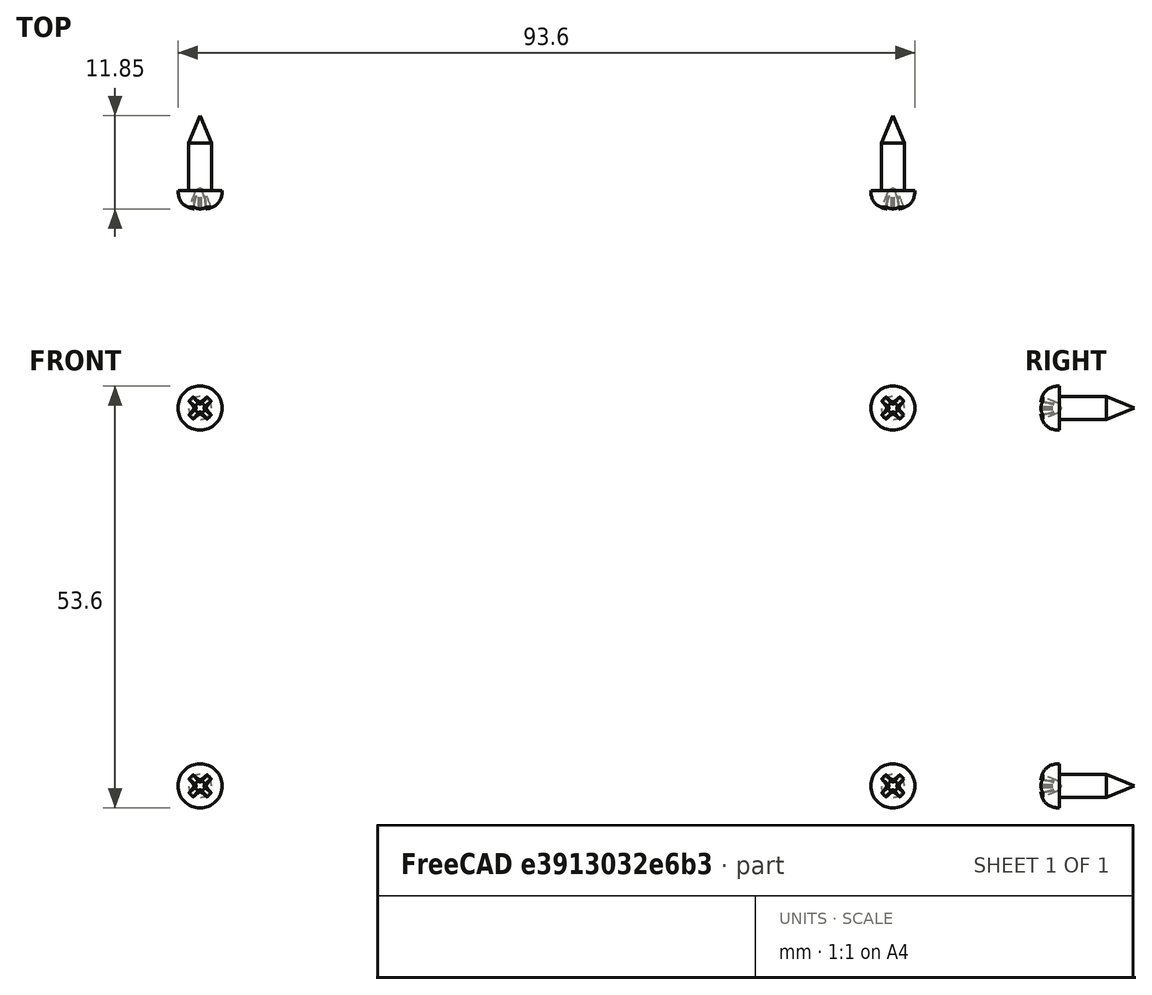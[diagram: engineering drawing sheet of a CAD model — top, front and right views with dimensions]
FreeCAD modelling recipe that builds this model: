
FCSTD DOCUMENT  (FreeCAD 1.0R39319 (Git))
Label: Assy_V3Connector_Board
License: All rights reserved
LicenseURL: https://en.wikipedia.org/wiki/All_rights_reserved
objects: TechDraw::DrawViewBalloon×6, Part::FeaturePython×4, TechDraw::DrawProjGroupItem×4, App::DocumentObjectGroup×3, TechDraw::DrawViewDimension×3, App::Link×2, TechDraw::DrawSVGTemplate×2, TechDraw::DrawPage×2, PartDesign::CoordinateSystem×1, App::FeaturePython×1, App::Part×1, Spreadsheet::Sheet×1, TechDraw::DrawViewSpreadsheet×1, TechDraw::DrawProjGroup×1
note: 11 computed .brp shape members not serialized (recipe doc carries the construction recipe); baked Part::Feature solids carry a one-line shape summary decoded from their .brp
EXTERNAL_REF file=../../Part/Print/ConnectorBoardv3_Carrier.FCStd obj=LCS_1
EXTERNAL_REF file=../../Part/Print/ConnectorBoardv3_Carrier.FCStd obj=Part
EXTERNAL_REF file=../../Part/Print/ConnectorBoardv3_Carrier.FCStd obj=LCS_2
EXTERNAL_REF file=../../Part/Purchase/V3_Connector_board.FCStd obj=LCS_1
EXTERNAL_REF file=../../Part/Purchase/V3_Connector_board.FCStd obj=V3_Connector_Only_1

FEATURE [App::DocumentObjectGroup] Parts
FEATURE [PartDesign::CoordinateSystem] LCS_Origin
  AttacherType = Attacher::AttachEngine3D
  AttachmentSupport = -> [X_Axis]
  MapMode = 2
FEATURE [App::DocumentObjectGroup] Constraints
FEATURE [App::FeaturePython] Variables  # WARN: FeaturePython — macro-defined, semantics opaque (R4)
  Type = App::PropertyContainer
FEATURE [App::DocumentObjectGroup] Configurations
FEATURE [App::Link] ConnectorBoardv3_Carrier
  AttachedBy = #LCS_1
  AttachedTo = Parent Assembly#LCS_Origin
  LinkedObject = -> <external ../../Part/Print/ConnectorBoardv3_Carrier.FCStd>#Part
  SolverId = Asm4EE
  expr: Placement = LCS_Origin.Placement * AttachmentOffset * ConnectorBoardv3_Carrier#LCS_1.Placement ^ -1
FEATURE [App::Link] V3_Connector_Only_1  label="V3 Connector Only 1"
  AttachedBy = #LCS_1
  AttachedTo = ConnectorBoardv3_Carrier#LCS_2
  AttachmentOffset = pos=(0,0,0) rot=(0.707107,-0.707107,0;3.14159rad)
  LinkPlacement = pos=(-50.0123,-11.5506,-30.0106) rot=(-0.57735,0.57735,-0.57735;4.18879rad)
  LinkedObject = -> <external ../../Part/Purchase/V3_Connector_board.FCStd>#V3_Connector_Only_1
  Placement = pos=(-50.0123,-11.5506,-30.0106) rot=(-0.57735,0.57735,-0.57735;4.18879rad)
  SolverId = Asm4EE
  expr: Placement = ConnectorBoardv3_Carrier.Placement * ConnectorBoardv3_Carrier#LCS_2.Placement * AttachmentOffset * V3_Connector_board#LCS_1.Placement ^ -1
FEATURE [Part::FeaturePython] Screw  label="ST2.9x9.5-Screw"  # WARN: FeaturePython — macro-defined, semantics opaque (R4)
  BaseObject = -> V3_Connector_Only_1 [Part__Feature388.Edge261]
  Diameter = 2
  Invert = false
  LeftHanded = false
  Length = 1
  LengthCustom = 9.5
  MatchOuter = false
  OffsetAngle = 0
  Placement = pos=(-44,-12.3124,-24) rot=(1,0,0;1.5708rad)
  Thread = false
  Type = 81
FEATURE [Part::FeaturePython] Screw001  label="ST2.9x9.5-Screw004"  # WARN: FeaturePython — macro-defined, semantics opaque (R4)
  BaseObject = -> V3_Connector_Only_1 [Part__Feature388.Edge17]
  Diameter = 2
  Invert = false
  LeftHanded = false
  Length = 1
  LengthCustom = 9.5
  MatchOuter = false
  OffsetAngle = 0
  Placement = pos=(44,-12.3124,-24) rot=(1,0,0;1.5708rad)
  Thread = false
  Type = 81
FEATURE [Part::FeaturePython] Screw002  label="ST2.9x9.5-Screw005"  # WARN: FeaturePython — macro-defined, semantics opaque (R4)
  BaseObject = -> V3_Connector_Only_1 [Part__Feature388.Edge18]
  Diameter = 2
  Invert = false
  LeftHanded = false
  Length = 1
  LengthCustom = 9.5
  MatchOuter = false
  OffsetAngle = 0
  Placement = pos=(44,-12.3124,24) rot=(1,0,0;1.5708rad)
  Thread = false
  Type = 81
FEATURE [Part::FeaturePython] Screw003  label="ST2.9x9.5-Screw006"  # WARN: FeaturePython — macro-defined, semantics opaque (R4)
  BaseObject = -> V3_Connector_Only_1 [Part__Feature388.Edge262]
  Diameter = 2
  Invert = false
  LeftHanded = false
  Length = 1
  LengthCustom = 9.5
  MatchOuter = false
  OffsetAngle = 0
  Placement = pos=(-44,-12.3124,24) rot=(1,0,0;1.5708rad)
  Thread = false
  Type = 81
FEATURE [App::Part] Assembly  label="Assy_V3Connector_Board"
  AssemblyType = Part::Link
  Group = -> [LCS_Origin,Constraints,Variables,Configurations,ConnectorBoardv3_Carrier,V3_Connector_Only_1,Screw,Screw001,Screw002,Screw003]
  Origin = -> Origin
  Type = Assembly
FEATURE [Spreadsheet::Sheet] Spreadsheet  label="BOM"
  cells = A1=3; B1=4; C1='M3x10 mm self-tapping screw; D1='5-10 mm; A2=2; B2=1; C2='ConnectorBoardv3; D2='-; A3=1; B3=1; C3='ConnectorBoardv3_Carrier; D3='-; E3='PETG or PLA; A4='Position; B4='Quantity; C4='Part; D4='Dimensions; E4='Material
FEATURE [TechDraw::DrawSVGTemplate] Template
  EditableTexts = approval_person=GitHub PR; creator=Stefan; date_of_issue=20.03.2026; document_type=Assembly Drawing; general_tolerances=na; identification_number=na; language_code=EN; part_material=na; revision_index=AAA; scale=1 : 1; sheet_number=1 / 1; title=Assy_V3Connector_Board
  Height = 297
  Orientation = 0
  Template = <userpath>/Documents/PiTrac/3D Printed Parts/Enclosure Version 3/Assets/PiTrac_A4_Portrait_ISO5457_minimal.svg
  Width = 210
FEATURE [TechDraw::DrawViewSpreadsheet] Sheet
  CellEnd = E4
  CellStart = A1
  Font = osifont
  LineWidth = 0.35
  LockPosition = false
  Rotation = 0
  ScaleType = 2
  Source = -> Spreadsheet
  Symbol = <blob: 4591 chars omitted>
  TextSize = 12
  X = 115.863
  Y = 88.338
FEATURE [TechDraw::DrawProjGroupItem] View  label="Front"
  CoarseView = false
  Direction = (0,-1,0)
  Focus = 100
  HardHidden = false
  IsoCount = 0
  IsoHidden = false
  IsoVisible = false
  LockPosition = true
  Perspective = false
  Rotation = 0
  RotationVector = (1,0,0)
  ScaleType = 2
  ScrubCount = 1
  SeamHidden = false
  SeamVisible = false
  SmoothHidden = false
  SmoothVisible = true
  Source = -> [Assembly]
  Type = 0
  X = 0
  XDirection = (1,0,0)
  Y = 0
FEATURE [TechDraw::DrawProjGroupItem] View001
  CoarseView = false
  Direction = (0.57735,-0.57735,-0.57735)
  Focus = 100
  HardHidden = false
  IsoCount = 0
  IsoHidden = false
  IsoVisible = false
  LockPosition = false
  Perspective = false
  Rotation = 0
  RotationVector = (1,0,0)
  Scale = 0.5
  ScaleType = 2
  ScrubCount = 1
  SeamHidden = false
  SeamVisible = false
  SmoothHidden = false
  SmoothVisible = true
  Source = -> [Assembly]
  Type = 0
  X = 158.895
  XDirection = (0.707107,0,0.707107)
  Y = 134.295
FEATURE [TechDraw::DrawViewBalloon] Balloon
  BubbleShape = 0
  EndType = 0
  EndTypeScale = 1
  KinkLength = 5
  LockPosition = false
  OriginX = -52.3797
  OriginY = -28.3457
  Rotation = 0
  ScaleType = 0
  ShapeScale = 1
  SourceView = -> View
  Text = 1
  TextWrapLen = -1
  X = -42.9122
  Y = -45
FEATURE [TechDraw::DrawViewBalloon] Balloon001
  BubbleShape = 0
  EndType = 0
  EndTypeScale = 1
  KinkLength = 5
  LockPosition = false
  OriginX = 21.9174
  OriginY = -1.30268
  Rotation = 0
  ScaleType = 0
  ShapeScale = 1
  SourceView = -> View
  Text = 2
  TextWrapLen = -1
  X = 31.9542
  Y = -45
FEATURE [TechDraw::DrawViewBalloon] Balloon002
  BubbleShape = 0
  EndType = 0
  EndTypeScale = 1
  KinkLength = 5
  LockPosition = false
  OriginX = -43.5551
  OriginY = 18.9084
  Rotation = 0
  ScaleType = 0
  ShapeScale = 1
  SourceView = -> View
  Text = 3
  TextWrapLen = -1
  X = -23.5551
  Y = 45
FEATURE [TechDraw::DrawViewBalloon] Balloon003
  BubbleShape = 0
  EndType = 0
  EndTypeScale = 1
  KinkLength = 5
  LockPosition = false
  OriginX = 44.2277
  OriginY = 19.5981
  Rotation = 0
  ScaleType = 0
  ShapeScale = 1
  SourceView = -> View
  Text = 3
  TextWrapLen = -1
  X = 64.2277
  Y = 45
FEATURE [TechDraw::DrawViewBalloon] Balloon005
  BubbleShape = 0
  EndType = 0
  EndTypeScale = 1
  KinkLength = 5
  LockPosition = false
  OriginX = -43.4289
  OriginY = -28.7897
  Rotation = 0
  ScaleType = 0
  ShapeScale = 1
  SourceView = -> View
  Text = 3
  TextWrapLen = -1
  X = -15.4584
  Y = -45
FEATURE [TechDraw::DrawViewBalloon] Balloon006
  BubbleShape = 0
  EndType = 0
  EndTypeScale = 1
  KinkLength = 5
  LockPosition = false
  OriginX = 44.6905
  OriginY = -29.4843
  Rotation = 0
  ScaleType = 0
  ShapeScale = 1
  SourceView = -> View
  Text = 3
  TextWrapLen = -1
  X = 64.6905
  Y = -9.48434
FEATURE [TechDraw::DrawProjGroupItem] ProjItem  label="Left"
  CoarseView = false
  Direction = (-1,-1e-16,0)
  Focus = 100
  HardHidden = false
  IsoCount = 0
  IsoHidden = false
  IsoVisible = false
  LockPosition = false
  Perspective = false
  Rotation = 0
  RotationVector = (1,0,0)
  ScaleType = 0
  ScrubCount = 1
  SeamHidden = false
  SeamVisible = false
  SmoothHidden = false
  SmoothVisible = true
  Source = -> [Assembly]
  Type = 1
  X = 26.9737
  XDirection = (1e-16,-1,0)
  Y = 0
FEATURE [TechDraw::DrawProjGroup] ProjGroup
  Anchor = -> View
  AutoDistribute = true
  LockPosition = false
  ProjectionType = 0
  Rotation = 0
  ScaleType = 0
  Source = -> [Assembly]
  Views = -> [View,ProjItem]
  X = 83.6926
  Y = 220.778
  spacingX = 15
  spacingY = 15
FEATURE [TechDraw::DrawViewDimension] Dimension
  AngleOverride = false
  Arbitrary = false
  ArbitraryTolerances = false
  BoxCorners = (2) [(-55,-35.0053,-1e-07),(55,35.0053,1e-07)]
  EqualTolerance = true
  ExtensionAngle = 0
  FormatSpec = %.2w
  FormatSpecOverTolerance = %+.2w
  FormatSpecUnderTolerance = %+.2w
  Inverted = false
  LineAngle = 0
  LockPosition = false
  MeasureType = 1
  OverTolerance = 0
  References2D = -> [View]
  Rotation = 0
  ScaleType = 0
  TheoreticalExact = false
  Type = 0
  UnderTolerance = 0
  X = 0
  Y = -54.1451
FEATURE [TechDraw::DrawViewDimension] Dimension001
  AngleOverride = false
  Arbitrary = false
  ArbitraryTolerances = false
  BoxCorners = (2) [(-11.9737,-35.0053,-1e-07),(11.9737,35.0053,1e-07)]
  EqualTolerance = true
  ExtensionAngle = 0
  FormatSpec = %.2w
  FormatSpecOverTolerance = %+.2w
  FormatSpecUnderTolerance = %+.2w
  Inverted = false
  LineAngle = 0
  LockPosition = false
  MeasureType = 1
  OverTolerance = 0
  References2D = -> [ProjItem]
  Rotation = 0
  ScaleType = 0
  TheoreticalExact = false
  Type = 0
  UnderTolerance = 0
  X = 18.3809
  Y = 0.005286
FEATURE [TechDraw::DrawViewDimension] Dimension002
  AngleOverride = false
  Arbitrary = false
  ArbitraryTolerances = false
  BoxCorners = (2) [(-11.9737,-35.0053,-1e-07),(11.9737,35.0053,1e-07)]
  EqualTolerance = true
  ExtensionAngle = 0
  FormatSpec = %.2w
  FormatSpecOverTolerance = %+.2w
  FormatSpecUnderTolerance = %+.2w
  Inverted = false
  LineAngle = 0
  LockPosition = false
  MeasureType = 1
  OverTolerance = 0
  References2D = -> [ProjItem]
  Rotation = 0
  ScaleType = 0
  TheoreticalExact = false
  Type = 0
  UnderTolerance = 0
  X = -0.8
  Y = 50.6191
FEATURE [TechDraw::DrawPage] Page
  KeepUpdated = true
  NextBalloonIndex = 8
  ProjectionType = 0
  Template = -> Template
  Views = -> [Sheet,View001,Balloon,Balloon001,Balloon002,Balloon003,Balloon005,Balloon006,ProjGroup,Dimension,Dimension001,Dimension002]
FEATURE [TechDraw::DrawSVGTemplate] Template001
  Height = 210
  Orientation = 1
  Template = C:/Program Files/FreeCAD 1.0/data/Mod/TechDraw/Templates/Default_Template_A4_Landscape.svg
  Width = 297
FEATURE [TechDraw::DrawProjGroupItem] View002
  CoarseView = false
  Direction = (0.57735,-0.57735,-0.57735)
  Focus = 100
  HardHidden = false
  IsoCount = 0
  IsoHidden = false
  IsoVisible = false
  LockPosition = false
  Perspective = false
  Rotation = 0
  RotationVector = (1,0,0)
  Scale = 2
  ScaleType = 2
  ScrubCount = 1
  SeamHidden = false
  SeamVisible = false
  SmoothHidden = false
  SmoothVisible = true
  Source = -> [Assembly]
  Type = 0
  X = 148.5
  XDirection = (0.707107,0,0.707107)
  Y = 105
FEATURE [TechDraw::DrawPage] Page001
  KeepUpdated = true
  NextBalloonIndex = 1
  ProjectionType = 0
  Template = -> Template001
  Views = -> [View002]

RESOLVED EXTERNAL PARTS (link-assembly join: the EXTERNAL_REF files above that resolve inside this repo's crawl, each included once):
---- part ../../Part/Print/ConnectorBoardv3_Carrier.FCStd = doc fcstd_a96b8e3c4932 ----
FCSTD DOCUMENT  (FreeCAD 1.0R39319 (Git))
Label: ConnectorBoardv3_Carrier
License: All rights reserved
LicenseURL: https://en.wikipedia.org/wiki/All_rights_reserved
objects: Sketcher::SketchObject×8, PartDesign::Pocket×4, PartDesign::Pad×3, PartDesign::Fillet×3, PartDesign::Mirrored×2, PartDesign::LinearPattern×2, PartDesign::CoordinateSystem×2, PartDesign::Hole×1, PartDesign::Body×1, App::Part×1
note: 60 computed .brp shape members not serialized (recipe doc carries the construction recipe); baked Part::Feature solids carry a one-line shape summary decoded from their .brp

FEATURE [Sketcher::SketchObject] Sketch
  ArcFitTolerance = 1e-06
  AttachmentSupport = -> [XZ_Plane001]
  FullyConstrained = true
  MakeInternals = false
  MapMode = 5
  Placement = pos=(0,0,0) rot=(1,0,0;1.5708rad)
  sketch-geometry (4):
    g0: LineSegment StartX=0 StartY=30 StartZ=0 EndX=0 EndY=0 EndZ=0
    g1: LineSegment StartX=0 StartY=0 StartZ=0 EndX=55 EndY=0 EndZ=0
    g2: LineSegment StartX=55 StartY=0 StartZ=0 EndX=55 EndY=30 EndZ=0
    g3: LineSegment StartX=55 StartY=30 StartZ=0 EndX=0 EndY=30 EndZ=0
  constraints (12):
    c: Coincident(g0,g1)
    c: Coincident(g1,g2)
    c: Coincident(g2,g3)
    c: Coincident(g3,g0)
    c: Vertical(g0)
    c: Vertical(g2)
    c: Distance(g-1,g2) = 55
    c: Distance(g0,g1) = 30
    c: Horizontal(g1)
    c: Horizontal(g3)
    c: DistanceX(g-1,g0) = 0
    c: DistanceY(g-1,g0) = 0
FEATURE [PartDesign::Pad] Pad
  Direction = (0,-1,2e-16)
  Length = 2.5
  Length2 = 10
  Placement = pos=(0,0,0) rot=(1,0,0;1.5708rad)
  Profile = -> Sketch
  ReferenceAxis = -> Sketch [N_Axis]
  Refine = true
  Suppressed = false
  Type = 0
FEATURE [Sketcher::SketchObject] Sketch001
  ArcFitTolerance = 1e-06
  AttachmentSupport = -> [XZ_Plane001]
  FullyConstrained = true
  MakeInternals = false
  MapMode = 5
  Placement = pos=(0,0,0) rot=(1,0,0;1.5708rad)
  sketch-geometry (1):
    g0: Circle CenterX=44 CenterY=24 CenterZ=0 NormalX=0 NormalY=0 NormalZ=1 AngleXU=0 Radius=3.75
  constraints (3):
    c: Diameter(g0) = 7.5
    c: DistanceX(g-1,g0) = 44
    c: Distance(g0,g-1) = 24
FEATURE [PartDesign::Pad] Pad001
  BaseFeature = -> Pad
  Direction = (0,-1,2e-16)
  Length = 11.5
  Length2 = 10
  Placement = pos=(0,0,0) rot=(1,0,0;1.5708rad)
  Profile = -> Sketch001
  ReferenceAxis = -> Sketch001 [N_Axis]
  Refine = true
  Suppressed = false
  Type = 0
FEATURE [PartDesign::Hole] Hole
  BaseFeature = -> Pad001
  CustomThreadClearance = 0
  Depth = 128.667
  DepthType = 1
  Diameter = 2.3
  DrillForDepth = false
  DrillPoint = 1
  DrillPointAngle = 118
  HoleCutCountersinkAngle = 90
  HoleCutCustomValues = false
  HoleCutDepth = 0
  HoleCutDiameter = 6.1
  HoleCutType = 0
  ModelThread = false
  Placement = pos=(0,0,0) rot=(1,0,0;1.5708rad)
  Profile = -> Pad001 [Face7]
  Refine = true
  Suppressed = false
  Tapered = false
  TaperedAngle = 90
  ThreadClass = 0
  ThreadDepth = 128.667
  ThreadDepthType = 0
  ThreadDirection = 0
  ThreadFit = 0
  ThreadSize = 0
  ThreadType = 0
  Threaded = false
  UseCustomThreadClearance = false
FEATURE [PartDesign::Fillet] Fillet
  Base = -> Hole [Edge5]
  BaseFeature = -> Hole
  Placement = pos=(0,0,0) rot=(1,0,0;1.5708rad)
  Radius = 3.5
  Refine = true
  SupportTransform = false
  Suppressed = false
  UseAllEdges = false
FEATURE [Sketcher::SketchObject] Sketch002
  ArcFitTolerance = 1e-06
  AttachmentSupport = -> [XZ_Plane001]
  FullyConstrained = true
  MakeInternals = false
  MapMode = 5
  Placement = pos=(0,0,0) rot=(1,0,0;1.5708rad)
  sketch-geometry (4):
    g0: ArcOfCircle CenterX=0 CenterY=0 CenterZ=0 NormalX=0 NormalY=0 NormalZ=1 AngleXU=0 Radius=4 StartAngle=1.5708 EndAngle=4.71239
    g1: ArcOfCircle CenterX=46 CenterY=-2e-16 CenterZ=0 NormalX=0 NormalY=0 NormalZ=1 AngleXU=0 Radius=4 StartAngle=4.71239 EndAngle=7.85398
    g2: LineSegment StartX=-6e-16 StartY=4 StartZ=0 EndX=46 EndY=4 EndZ=0
    g3: LineSegment StartX=-7e-16 StartY=-4 StartZ=0 EndX=46 EndY=-4 EndZ=0
  constraints (9):
    c: Tangent(g0,g2) = 1.5708
    c: Tangent(g0,g3) = -1.5708
    c: Tangent(g1,g2) = 1.5708
    c: Tangent(g1,g3) = -1.5708
    c: Equal(g0,g1)
    c: Horizontal(g3)
    c: Coincident(g0,g-1)
    c: DistanceY(g0,g0) = 4
    c: DistanceX(g3,g3) = 46
FEATURE [PartDesign::Pocket] Pocket
  BaseFeature = -> Fillet
  Direction = (0,1,-2e-16)
  Length = 5
  Length2 = 5
  Placement = pos=(0,0,0) rot=(1,0,0;1.5708rad)
  Profile = -> Sketch002
  ReferenceAxis = -> Sketch002 [N_Axis]
  Refine = true
  Reversed = true
  Suppressed = false
  Type = 1
FEATURE [PartDesign::Mirrored] Mirrored
  BaseFeature = -> Pocket
  MirrorPlane = -> XY_Plane001
  Placement = pos=(0,0,0) rot=(1,0,0;1.5708rad)
  Refine = true
  Suppressed = false
  TransformMode = 1
FEATURE [PartDesign::LinearPattern] LinearPattern
  BaseFeature = -> Mirrored
  Direction = -> Z_Axis001
  Length = 16
  Mode = 0
  Occurrences = 2
  Offset = 16
  Originals = -> [Pocket]
  Placement = pos=(0,0,0) rot=(1,0,0;1.5708rad)
  Refine = true
  Suppressed = false
  TransformMode = 0
FEATURE [PartDesign::LinearPattern] LinearPattern001
  BaseFeature = -> LinearPattern
  Direction = -> Z_Axis001
  Length = 16
  Mode = 0
  Occurrences = 2
  Offset = 16
  Originals = -> [Pocket]
  Placement = pos=(0,0,0) rot=(1,0,0;1.5708rad)
  Refine = true
  Reversed = true
  Suppressed = false
  TransformMode = 0
FEATURE [PartDesign::Mirrored] Mirrored001
  BaseFeature = -> LinearPattern001
  MirrorPlane = -> YZ_Plane001
  Placement = pos=(0,0,0) rot=(1,0,0;1.5708rad)
  Refine = true
  Suppressed = false
  TransformMode = 1
FEATURE [Sketcher::SketchObject] Sketch003
  ArcFitTolerance = 1e-06
  AttachmentSupport = -> [Mirrored001]
  ExternalGeometry = -> [Mirrored001]
  FullyConstrained = true
  MakeInternals = false
  MapMode = 5
  Placement = pos=(0,-2.5,0) rot=(1,0,0;1.5708rad)
  sketch-geometry (8):
    g0: LineSegment StartX=-50 StartY=40 StartZ=0 EndX=-50 EndY=30 EndZ=0
    g1: LineSegment StartX=-50 StartY=30 StartZ=0 EndX=-30 EndY=30 EndZ=0
    g2: LineSegment StartX=-30 StartY=30 StartZ=0 EndX=-30 EndY=40 EndZ=0
    g3: LineSegment StartX=-30 StartY=40 StartZ=0 EndX=-50 EndY=40 EndZ=0
    g4: LineSegment StartX=30 StartY=40 StartZ=0 EndX=30 EndY=30 EndZ=0
    g5: LineSegment StartX=30 StartY=30 StartZ=0 EndX=50 EndY=30 EndZ=0
    g6: LineSegment StartX=50 StartY=30 StartZ=0 EndX=50 EndY=40 EndZ=0
    g7: LineSegment StartX=50 StartY=40 StartZ=0 EndX=30 EndY=40 EndZ=0
  constraints (23):
    c: Coincident(g0,g1)
    c: Coincident(g1,g2)
    c: Coincident(g2,g3)
    c: Coincident(g3,g0)
    c: Vertical(g0)
    c: Vertical(g2)
    c: Horizontal(g1)
    c: Horizontal(g3)
    c: Coincident(g4,g5)
    c: Coincident(g5,g6)
    c: Coincident(g6,g7)
    c: Coincident(g7,g4)
    c: Vertical(g4)
    c: Vertical(g6)
    c: Horizontal(g5)
    c: Horizontal(g7)
    c: Distance(g1,g3) = 10
    c: Distance(g5,g7) = 10
    c: Distance(g2,g0) = 20
    c: Distance(g6,g4) = 20
    c: PointOnObject(g1,g-3)
    c: DistanceX(g0,g6) = 100
    c: Symmetric(g2,g4,g-2)
FEATURE [PartDesign::Pad] Pad002
  BaseFeature = -> Mirrored001
  Direction = (0,-1,2e-16)
  Length = 10
  Length2 = 10
  Placement = pos=(0,0,0) rot=(1,0,0;1.5708rad)
  Profile = -> Sketch003
  ReferenceAxis = -> Sketch003 [N_Axis]
  Refine = true
  Suppressed = false
  Type = 3
  UpToFace = -> Mirrored001 [Face8]
FEATURE [Sketcher::SketchObject] Sketch004
  ArcFitTolerance = 1e-06
  AttachmentSupport = -> [Pad002]
  ExternalGeometry = -> [Pad002]
  FullyConstrained = true
  MakeInternals = false
  MapMode = 5
  Placement = pos=(0,-2.5,8e-16) rot=(1,0,0;1.5708rad)
  sketch-geometry (6):
    g0: Circle CenterX=-46.458 CenterY=36.5 CenterZ=0 NormalX=0 NormalY=0 NormalZ=1 AngleXU=0 Radius=1.5
    g1: Circle CenterX=-40.9807 CenterY=36 CenterZ=0 NormalX=0 NormalY=0 NormalZ=1 AngleXU=0 Radius=2
    g2: Circle CenterX=-34.5 CenterY=35.5 CenterZ=0 NormalX=0 NormalY=0 NormalZ=1 AngleXU=0 Radius=2.5
    g3: Circle CenterX=45.458 CenterY=35.5 CenterZ=0 NormalX=0 NormalY=0 NormalZ=1 AngleXU=0 Radius=2.5
    g4: Circle CenterX=38.9772 CenterY=36 CenterZ=0 NormalX=0 NormalY=0 NormalZ=1 AngleXU=0 Radius=2
    g5: Circle CenterX=33.5 CenterY=36.5 CenterZ=0 NormalX=0 NormalY=0 NormalZ=1 AngleXU=0 Radius=1.5
  constraints (18):
    c: Diameter(g2) = 5
    c: Diameter(g1) = 4
    c: Diameter(g0) = 3
    c: Distance(g2,g-5) = 2
    c: Distance(g1,g-5) = 2
    c: Distance(g0,g-5) = 2
    c: Distance(g2,g-3) = 2
    c: Distance(g1,g2) = 2
    c: Distance(g0,g1) = 2
    c: Diameter(g3) = 5
    c: Diameter(g4) = 4
    c: Diameter(g5) = 3
    c: Distance(g3,g-6) = 2
    c: Distance(g4,g-6) = 2
    c: Distance(g5,g-6) = 2
    c: Distance(g5,g-7) = 2
    c: Distance(g5,g4) = 2
    c: Distance(g4,g3) = 2
FEATURE [PartDesign::Pocket] Pocket001
  BaseFeature = -> Pad002
  Direction = (0,1,-2e-16)
  Length = 5
  Length2 = 5
  Placement = pos=(0,0,0) rot=(1,0,0;1.5708rad)
  Profile = -> Sketch004
  ReferenceAxis = -> Sketch004 [N_Axis]
  Refine = true
  Suppressed = false
  Type = 0
FEATURE [Sketcher::SketchObject] Sketch005
  ArcFitTolerance = 1e-06
  AttachmentSupport = -> [Pocket001]
  ExternalGeometry = -> [Pocket001]
  FullyConstrained = true
  MakeInternals = false
  MapMode = 5
  Placement = pos=(0,-2.5,8e-16) rot=(1,0,0;1.5708rad)
  sketch-geometry (24):
    g0: LineSegment StartX=-35.75 StartY=40 StartZ=0 EndX=-35.75 EndY=35.5 EndZ=0
    g1: LineSegment StartX=-35.75 StartY=35.5 StartZ=0 EndX=-33.25 EndY=35.5 EndZ=0
    g2: LineSegment StartX=-33.25 StartY=35.5 StartZ=0 EndX=-33.25 EndY=40 EndZ=0
    g3: LineSegment StartX=-33.25 StartY=40 StartZ=0 EndX=-35.75 EndY=40 EndZ=0
    g4: LineSegment StartX=-41.9807 StartY=40 StartZ=0 EndX=-41.9807 EndY=36 EndZ=0
    g5: LineSegment StartX=-41.9807 StartY=36 StartZ=0 EndX=-39.9807 EndY=36 EndZ=0
    g6: LineSegment StartX=-39.9807 StartY=36 StartZ=0 EndX=-39.9807 EndY=40 EndZ=0
    g7: LineSegment StartX=-39.9807 StartY=40 StartZ=0 EndX=-41.9807 EndY=40 EndZ=0
    g8: LineSegment StartX=-47.208 StartY=40 StartZ=0 EndX=-47.208 EndY=36.5 EndZ=0
    g9: LineSegment StartX=-47.208 StartY=36.5 StartZ=0 EndX=-45.708 EndY=36.5 EndZ=0
    g10: LineSegment StartX=-45.708 StartY=36.5 StartZ=0 EndX=-45.708 EndY=40 EndZ=0
    g11: LineSegment StartX=-45.708 StartY=40 StartZ=0 EndX=-47.208 EndY=40 EndZ=0
    g12: LineSegment StartX=32.75 StartY=40 StartZ=0 EndX=32.75 EndY=36.5 EndZ=0
    g13: LineSegment StartX=32.75 StartY=36.5 StartZ=0 EndX=34.25 EndY=36.5 EndZ=0
    g14: LineSegment StartX=34.25 StartY=36.5 StartZ=0 EndX=34.25 EndY=40 EndZ=0
    g15: LineSegment StartX=34.25 StartY=40 StartZ=0 EndX=32.75 EndY=40 EndZ=0
    g16: LineSegment StartX=37.9772 StartY=40 StartZ=0 EndX=37.9772 EndY=36 EndZ=0
    g17: LineSegment StartX=37.9772 StartY=36 StartZ=0 EndX=39.9772 EndY=36 EndZ=0
    g18: LineSegment StartX=39.9772 StartY=36 StartZ=0 EndX=39.9772 EndY=40 EndZ=0
    g19: LineSegment StartX=39.9772 StartY=40 StartZ=0 EndX=37.9772 EndY=40 EndZ=0
    g20: LineSegment StartX=44.208 StartY=40 StartZ=0 EndX=44.208 EndY=35.5 EndZ=0
    g21: LineSegment StartX=44.208 StartY=35.5 StartZ=0 EndX=46.708 EndY=35.5 EndZ=0
    g22: LineSegment StartX=46.708 StartY=35.5 StartZ=0 EndX=46.708 EndY=40 EndZ=0
    g23: LineSegment StartX=46.708 StartY=40 StartZ=0 EndX=44.208 EndY=40 EndZ=0
  constraints (66):
    c: Coincident(g0,g1)
    c: Coincident(g1,g2)
    c: Coincident(g2,g3)
    c: Coincident(g3,g0)
    c: Vertical(g0)
    c: Vertical(g2)
    c: Horizontal(g1)
    c: Horizontal(g3)
    c: Coincident(g4,g5)
    c: Coincident(g5,g6)
    c: Coincident(g6,g7)
    c: Coincident(g7,g4)
    c: Vertical(g4)
    c: Vertical(g6)
    c: Horizontal(g5)
    c: Horizontal(g7)
    c: Coincident(g8,g9)
    c: Coincident(g9,g10)
    c: Coincident(g10,g11)
    c: Coincident(g11,g8)
    c: Vertical(g8)
    c: Vertical(g10)
    c: Horizontal(g9)
    c: Horizontal(g11)
    c: PointOnObject(g2,g-3)
    c: PointOnObject(g6,g-3)
    c: PointOnObject(g10,g-3)
    c: Symmetric(g8,g9,g-6)
    c: Symmetric(g4,g5,g-5)
    c: Symmetric(g0,g1,g-4)
    c: Distance(g3,g3) = 2.5
    c: DistanceX(g7,g7) = 2
    c: DistanceX(g11,g11) = 1.5
    c: Coincident(g12,g13)
    c: Coincident(g13,g14)
    c: Coincident(g14,g15)
    c: Coincident(g15,g12)
    c: Vertical(g12)
    c: Vertical(g14)
    c: Horizontal(g13)
    c: Horizontal(g15)
    c: PointOnObject(g12,g-7)
    c: Coincident(g16,g17)
    c: Coincident(g17,g18)
    c: Coincident(g18,g19)
    c: Coincident(g19,g16)
    c: Vertical(g16)
    c: Vertical(g18)
    c: Horizontal(g17)
    c: Horizontal(g19)
    c: PointOnObject(g16,g-7)
    c: Coincident(g20,g21)
    c: Coincident(g21,g22)
    c: Coincident(g22,g23)
    c: Coincident(g23,g20)
    c: Vertical(g20)
    c: Vertical(g22)
    c: Horizontal(g21)
    c: Horizontal(g23)
    c: PointOnObject(g20,g-7)
    c: Symmetric(g12,g13,g-8)
    c: Symmetric(g16,g17,g-9)
    c: Symmetric(g20,g21,g-10)
    c: DistanceX(g23,g23) = 2.5
    c: Distance(g19,g19) = 2
    c: DistanceX(g15,g15) = 1.5
FEATURE [PartDesign::Pocket] Pocket002
  BaseFeature = -> Pocket001
  Direction = (0,1,-2e-16)
  Length = 5
  Length2 = 5
  Placement = pos=(0,0,0) rot=(1,0,0;1.5708rad)
  Profile = -> Sketch005
  ReferenceAxis = -> Sketch005 [N_Axis]
  Refine = true
  Suppressed = false
  Type = 0
FEATURE [PartDesign::Fillet] Fillet001
  Base = -> Pocket002 [Edge3,Edge1]
  BaseFeature = -> Pocket002
  Placement = pos=(0,0,0) rot=(1,0,0;1.5708rad)
  Radius = 3.5
  Refine = true
  SupportTransform = false
  Suppressed = false
  UseAllEdges = false
FEATURE [PartDesign::Fillet] Fillet002
  Base = -> Fillet001 [Edge141,Edge167,Edge158,Edge165,Edge157,Edge150,Edge149,Edge169,Edge137,Edge138,Edge143,Edge151,Edge153,Edge159,Edge161,Edge163]
  BaseFeature = -> Fillet001
  Placement = pos=(0,0,0) rot=(1,0,0;1.5708rad)
  Radius = 1
  Refine = true
  SupportTransform = false
  Suppressed = false
  UseAllEdges = false
FEATURE [Sketcher::SketchObject] Sketch006
  ArcFitTolerance = 1e-06
  AttachmentSupport = -> [Fillet002]
  FullyConstrained = true
  MakeInternals = false
  MapMode = 5
  Placement = pos=(0,-2.5,8e-16) rot=(1,0,0;1.5708rad)
FEATURE [Sketcher::SketchObject] Sketch007
  ArcFitTolerance = 1e-06
  AttachmentSupport = -> [Fillet002]
  ExternalGeometry = -> [Fillet002]
  FullyConstrained = true
  MakeInternals = false
  MapMode = 5
  Placement = pos=(0,-2.5,8e-16) rot=(1,0,0;1.5708rad)
  sketch-geometry (20):
    g0: LineSegment StartX=-43.4807 StartY=30.5 StartZ=0 EndX=-41.4807 EndY=30.5 EndZ=0
    g1: LineSegment StartX=-41.4807 StartY=30.5 StartZ=0 EndX=-41.4807 EndY=32.5 EndZ=0
    g2: LineSegment StartX=-41.4807 StartY=32.5 StartZ=0 EndX=-40.4807 EndY=32.5 EndZ=0
    g3: LineSegment StartX=-40.4807 StartY=32.5 StartZ=0 EndX=-40.4807 EndY=30.5 EndZ=0
    g4: LineSegment StartX=-40.4807 StartY=30.5 StartZ=0 EndX=-38.4807 EndY=30.5 EndZ=0
    g5: LineSegment StartX=-38.4807 StartY=30.5 StartZ=0 EndX=-38.4807 EndY=29.5 EndZ=0
    g6: LineSegment StartX=-38.4807 StartY=29.5 StartZ=0 EndX=-40.4807 EndY=29.5 EndZ=0
    g7: LineSegment StartX=-40.4807 StartY=29.5 StartZ=0 EndX=-40.4807 EndY=27.5 EndZ=0
    g8: LineSegment StartX=-40.4807 StartY=27.5 StartZ=0 EndX=-41.4807 EndY=27.5 EndZ=0
    g9: LineSegment StartX=-41.4807 StartY=27.5 StartZ=0 EndX=-41.4807 EndY=29.5 EndZ=0
    g10: LineSegment StartX=-41.4807 StartY=29.5 StartZ=0 EndX=-43.4807 EndY=29.5 EndZ=0
    g11: LineSegment StartX=-43.4807 StartY=29.5 StartZ=0 EndX=-43.4807 EndY=30.5 EndZ=0
    g12: LineSegment [constr] StartX=-43.4807 StartY=30 StartZ=0 EndX=-38.4807 EndY=30 EndZ=0
    g13: LineSegment [constr] StartX=-40.9807 StartY=32.5 StartZ=0 EndX=-40.9807 EndY=27.5 EndZ=0
    g14: LineSegment StartX=36.4772 StartY=30.5 StartZ=0 EndX=36.4772 EndY=29.5 EndZ=0
    g15: LineSegment StartX=36.4772 StartY=29.5 StartZ=0 EndX=41.4772 EndY=29.5 EndZ=0
    g16: LineSegment StartX=41.4772 StartY=29.5 StartZ=0 EndX=41.4772 EndY=30.5 EndZ=0
    g17: LineSegment StartX=41.4772 StartY=30.5 StartZ=0 EndX=36.4772 EndY=30.5 EndZ=0
    g18: LineSegment [constr] StartX=36.4772 StartY=30 StartZ=0 EndX=41.4772 EndY=30 EndZ=0
    g19: LineSegment [constr] StartX=38.9772 StartY=30.5 StartZ=0 EndX=38.9772 EndY=29.5 EndZ=0
  constraints (56):
    c: Horizontal(g0)
    c: Coincident(g0,g1)
    c: Vertical(g1)
    c: Coincident(g1,g2)
    c: Coincident(g2,g3)
    c: Vertical(g3)
    c: Coincident(g3,g4)
    c: Horizontal(g4)
    c: Coincident(g4,g5)
    c: Coincident(g5,g6)
    c: Horizontal(g6)
    c: Coincident(g6,g7)
    c: Vertical(g7)
    c: Coincident(g7,g8)
    c: Horizontal(g8)
    c: Coincident(g8,g9)
    c: Vertical(g9)
    c: Coincident(g9,g10)
    c: Horizontal(g10)
    c: Coincident(g10,g11)
    c: Coincident(g11,g0)
    c: Vertical(g11)
    c: Vertical(g5)
    c: Horizontal(g2)
    c: PointOnObject(g3,g0)
    c: PointOnObject(g6,g10)
    c: PointOnObject(g0,g9)
    c: PointOnObject(g3,g7)
    c: Symmetric(g11,g11,g12)
    c: Symmetric(g5,g5,g12)
    c: Symmetric(g2,g2,g13)
    c: Symmetric(g8,g8,g13)
    c: DistanceX(g12,g12) = 5
    c: DistanceY(g13,g13) = 5
    c: Distance(g3,g1) = 1
    c: Distance(g6,g4) = 1
    c: Distance(g11,g13) = 2.5
    c: Distance(g12,g2) = 2.5
    c: PointOnObject(g12,g-3)
    c: PointOnObject(g-4,g13)
    c: Coincident(g14,g15)
    c: Coincident(g15,g16)
    c: Coincident(g16,g17)
    c: Coincident(g17,g14)
    c: Vertical(g14)
    c: Vertical(g16)
    c: Horizontal(g15)
    c: Horizontal(g17)
    c: Distance(g16,g14) = 5
    c: Distance(g17,g15) = 1
    c: Symmetric(g14,g14,g18)
    c: Symmetric(g16,g16,g18)
    c: Symmetric(g17,g17,g19)
    c: Symmetric(g15,g15,g19)
    c: PointOnObject(g-3,g18)
    c: PointOnObject(g-6,g19)
FEATURE [PartDesign::Pocket] Pocket003
  BaseFeature = -> Fillet002
  Direction = (0,1,-2e-16)
  Length = 5
  Length2 = 5
  Placement = pos=(0,0,0) rot=(1,0,0;1.5708rad)
  Profile = -> Sketch007
  ReferenceAxis = -> Sketch007 [N_Axis]
  Refine = true
  Suppressed = false
  Type = 0
FEATURE [PartDesign::Body] Body  label="ConnectorBoardv3_Carrier001"
  AllowCompound = false
  Group = -> [Sketch,Pad,Sketch001,Pad001,Hole,Fillet,Sketch002,Pocket,Mirrored,LinearPattern,LinearPattern001,Mirrored001,Sketch003,Pad002,Sketch004,Pocket001,Sketch005,Pocket002,Fillet001,Fillet002,Sketch006,Sketch007,Pocket003]
  Origin = -> Origin001
  Tip = -> Pocket003
FEATURE [PartDesign::CoordinateSystem] LCS_1
  AttacherType = Attacher::AttachEngine3D
FEATURE [PartDesign::CoordinateSystem] LCS_2
  AttacherType = Attacher::AttachEngine3D
  AttachmentSupport = -> [Pocket003]
  MapMode = 11
  Placement = pos=(-44,-11.5,24) rot=(0.57735,0.57735,0.57735;4.18879rad)
FEATURE [App::Part] Part  label="ConnectorBoardv3_Carrier"
  Group = -> [Body,LCS_1,LCS_2]
  Origin = -> Origin
